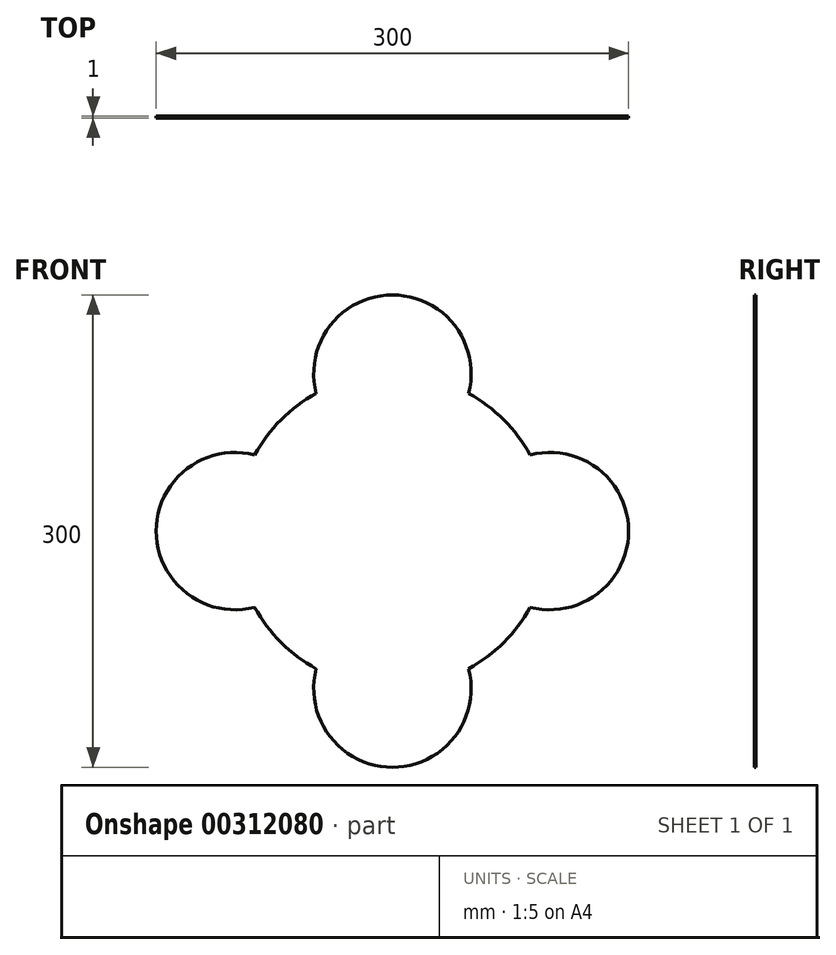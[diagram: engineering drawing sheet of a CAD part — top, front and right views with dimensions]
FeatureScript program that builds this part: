
annotation { "Feature Type Name" : "Feature", "Feature Type Description" : "" }
export const myFeature = defineFeature(function(context is Context, id is Id, definition is map)
    precondition{}
    {
        {
            var Q0;
            Q0=qCreatedBy(makeId("Front.planeOp"),FACE);
            var sketch = newSketch(context, id + "F0", { "sketchPlane" : qUnion([Q0])});
            skCircle(sketch, "E0", {"center": v(0, 0) * mm, "radius": 100 * mm});
            skSolve(sketch);
        }
        {
            var Q0;
            Q0 = qSketchRegion(id + "F0", true);
            extrude(context, id + "F1", {"entities" : qUnion([Q0]), "depth" : 1 * mm});
        }
        {
            var Q0;
            Q0=makeQuery(id+"F1.opExtrude","CAP_FACE",FACE,{"disambiguationData":[OSD([sQuery(id+"F0.wireOp",EDGE,"E0")])],"isStart":false});
            var sketch = newSketch(context, id + "F2", { "sketchPlane" : qUnion([Q0])});
            skCircle(sketch, "E1", {"center": v(-100, 0) * mm, "radius": 50 * mm});
            skCircle(sketch, "E2", {"center": v(0, 100) * mm, "radius": 50 * mm});
            skCircle(sketch, "E3", {"center": v(100, 0) * mm, "radius": 50 * mm});
            skCircle(sketch, "E4", {"center": v(0, -100) * mm, "radius": 50 * mm});
            skSolve(sketch);
        }
        {
            var Q0;
            Q0 = qSketchRegion(id + "F2", true);
            extrude(context, id + "F3", {"entities" : qUnion([Q0]), "operationType" : NewBodyOperationType.ADD, "oppositeDirection" : true, "depth" : 1 * mm});
        }
    });
